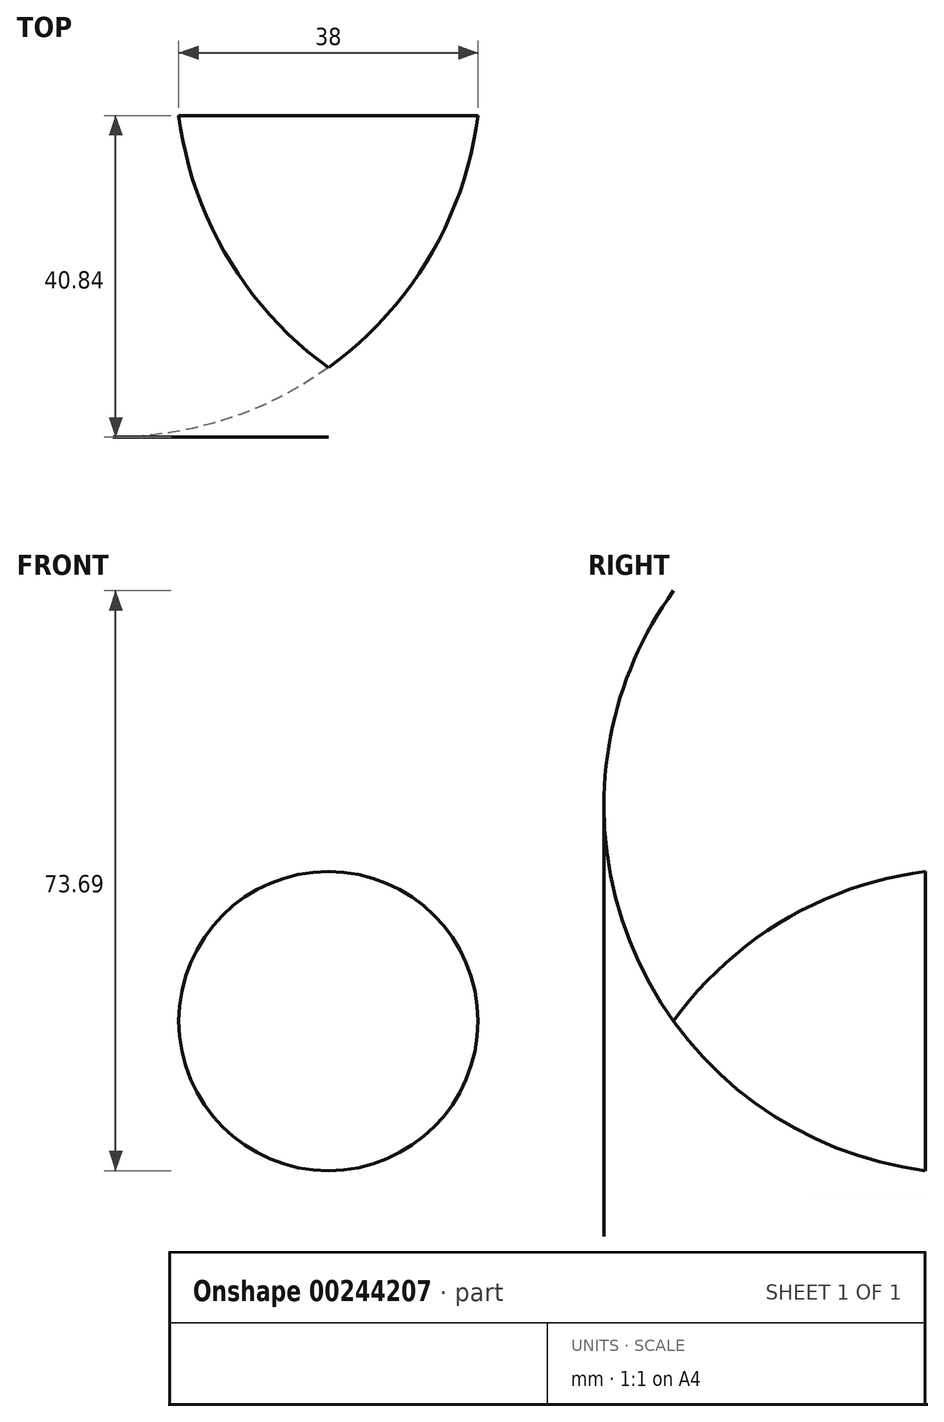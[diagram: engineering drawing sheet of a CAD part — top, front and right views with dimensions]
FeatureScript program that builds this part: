
annotation { "Feature Type Name" : "Feature", "Feature Type Description" : "" }
export const myFeature = defineFeature(function(context is Context, id is Id, definition is map)
    precondition{}
    {
        {
            var Q0;
            Q0=qCreatedBy(makeId("Right.planeOp"),FACE);
            var sketch = newSketch(context, id + "F0", { "sketchPlane" : qUnion([Q0])});
            skLineSegment(sketch, "E0", {"start": v(0, 0) * mm, "end": v(0, -19) * mm});
            skLineSegment(sketch, "E1", {"start": v(0, 0) * mm, "end": v(-32, 0) * mm});
            skArc(sketch, "E2", {"start": v(-32, 0) * mm, "mid": v(-17.97, -12.82) * mm, "end": v(0, -19) * mm});
            skSolve(sketch);
        }
        {
            var Q0;
            Q0 = qSketchRegion(id + "F0", true);
            var Q1;
            Q1=sQuery(id+"F0.wireOp",EDGE,"E1");
            revolve(context, id + "F1", {"entities" : qUnion([Q0]), "axis" : qUnion([Q1]), "revolveType" : RevolveType.FULL});
        }
    });
